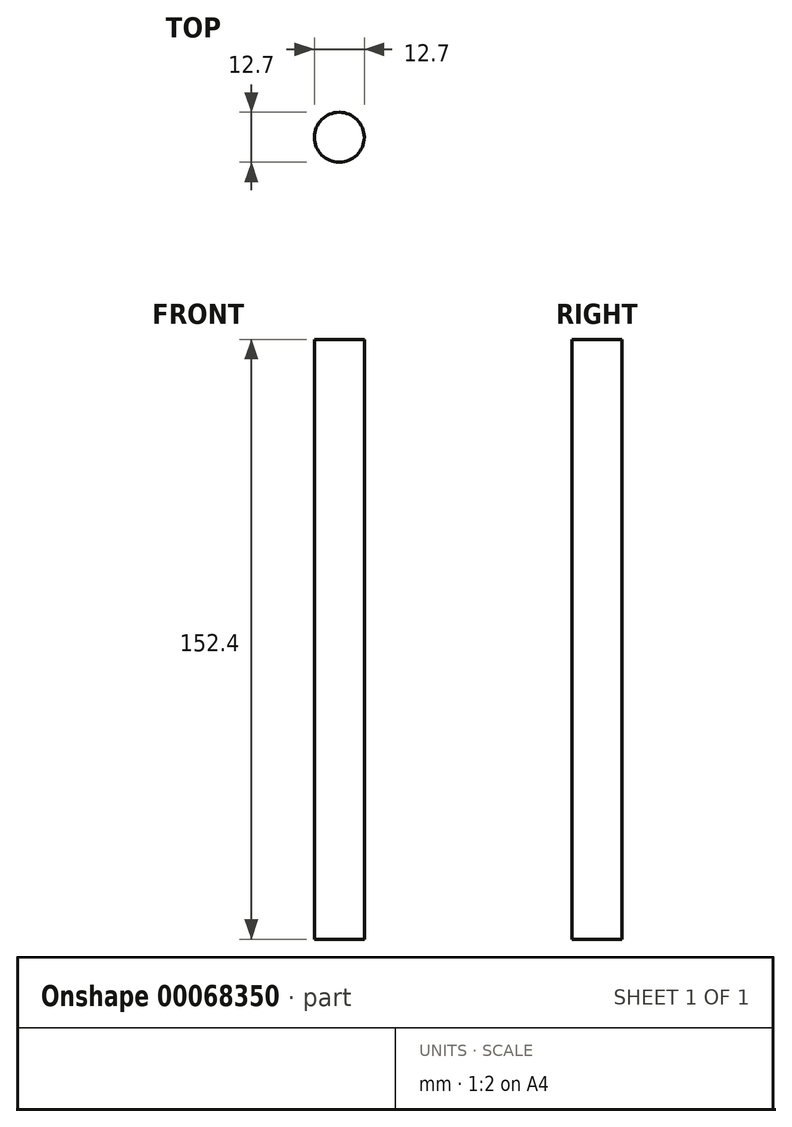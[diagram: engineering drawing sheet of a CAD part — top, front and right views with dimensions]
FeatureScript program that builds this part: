
annotation { "Feature Type Name" : "Feature", "Feature Type Description" : "" }
export const myFeature = defineFeature(function(context is Context, id is Id, definition is map)
    precondition{}
    {
        {
            var Q0;
            Q0=qCreatedBy(makeId("Top.planeOp"),FACE);
            var sketch = newSketch(context, id + "F0", { "sketchPlane" : qUnion([Q0])});
            skCircle(sketch, "E0", {"center": v(0, 0) * mm, "radius": 6.35 * mm});
            skSolve(sketch);
        }
        {
            var Q0;
            Q0 = qSketchRegion(id + "F0", true);
            extrude(context, id + "F1", {"entities" : qUnion([Q0]), "depth" : 152.4 * mm});
        }
    });
